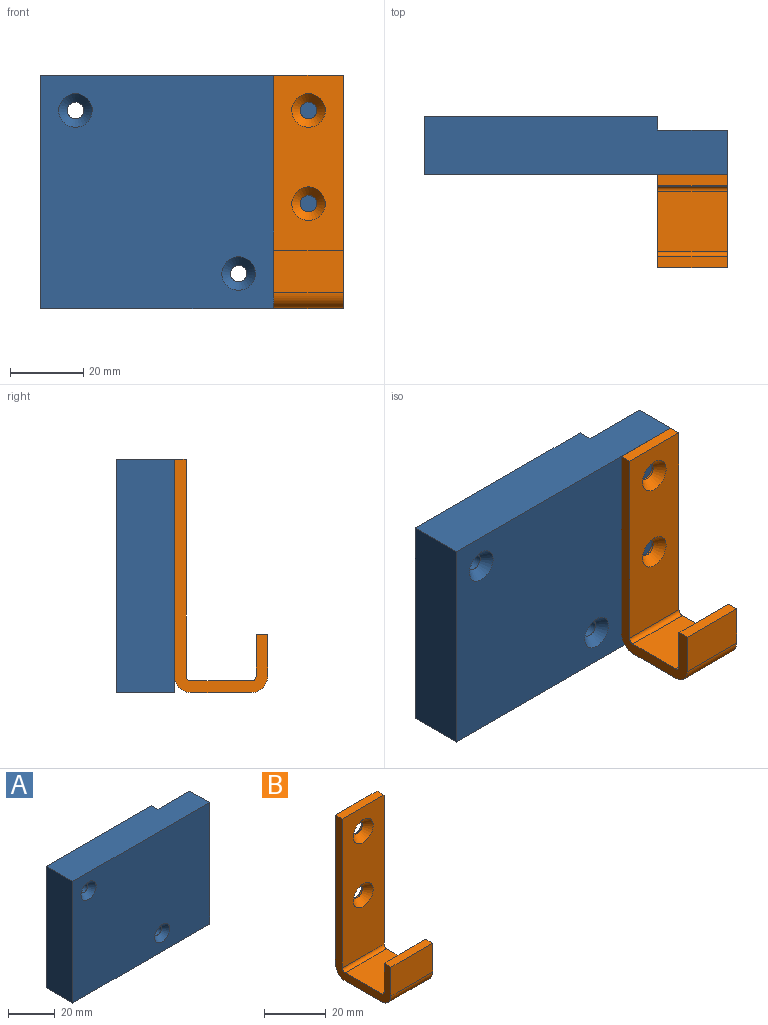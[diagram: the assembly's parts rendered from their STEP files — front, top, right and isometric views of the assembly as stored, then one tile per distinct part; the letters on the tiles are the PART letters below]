
ASSEMBLY  parts=2 mates=1
PART A: 12 faces, bbox 82.6x15.9x63.5 mm
  f0: plane 82.55x15.88mm, normal (0,0,1), area 1237.9mm2, adj f1,f3,f4,f5,f6,f7
  f1: plane 63.5x15.88mm, normal (-1,0,0), area 1008.1mm2, adj f0,f2,f4,f5
  f2: plane 82.55x15.88mm, normal (0,0,-1), area 1237.9mm2, adj f1,f3,f4,f5,f6,f7
  f3: plane 63.5x12.07mm, normal (1,0,0), area 766.1mm2, adj f0,f2,f4,f7
  f4: plane 82.55x63.5mm, normal (0,-1,0), area 5111.3mm2, adj f0,f1,f2,f3,f9,f11
  f5: plane 63.5x63.5mm, normal (0,1,0), area 4000.5mm2, adj f0,f1,f2,f6,f8,f10
  f6: plane 63.5x3.81mm, normal (1,0,0), area 241.9mm2, adj f0,f2,f5,f7
  f7: plane 63.5x19.05mm, normal (0,1,0), area 1209.7mm2, adj f0,f2,f3,f6
  f8: cylinder r=2.25mm len=13.22mm, axis (0,-1,0), area 186.7mm2, adj f5,f9
  f9: cone r=2.25mm half-angle=41deg, axis (0,-1,0), area 75.3mm2, adj f4,f8
  f10: cylinder r=2.25mm len=13.22mm, axis (0,-1,0), area 186.7mm2, adj f5,f11
  f11: cone r=2.25mm half-angle=41deg, axis (0,-1,0), area 75.3mm2, adj f4,f10
PART B: 18 faces, bbox 19.1x25.4x63.5 mm
  f0: cylinder r=1.27mm len=19.05mm, axis (-1,0,0), area 38mm2, adj f1,f11,f12,f13
  f1: plane 19.05x11.43mm, normal (0,1,0), area 217.7mm2, adj f0,f2,f12,f13
  f2: plane 19.05x3.18mm, normal (0,0,1), area 60.5mm2, adj f1,f3,f12,f13
  f3: plane 19.05x11.43mm, normal (0,-1,0), area 217.7mm2, adj f2,f4,f12,f13
  f4: cylinder r=4.45mm len=19.05mm, axis (-1,0,0), area 133mm2, adj f3,f5,f12,f13
  f5: plane 19.05x16.51mm, normal (0,0,-1), area 314.5mm2, adj f4,f6,f12,f13
  f6: cylinder r=4.45mm len=19.05mm, axis (-1,0,0), area 133mm2, adj f5,f7,f12,f13
  f7: plane 59.06x19.05mm, normal (0,1,0), area 1093.2mm2, adj f6,f8,f12,f13,f14,f16
  f8: plane 19.05x3.18mm, normal (0,0,1), area 60.5mm2, adj f7,f9,f12,f13
  f9: plane 59.06x19.05mm, normal (0,-1,0), area 994.4mm2, adj f8,f10,f12,f13,f15,f17
  f10: cylinder r=1.27mm len=19.05mm, axis (-1,0,0), area 38mm2, adj f9,f11,f12,f13
  f11: plane 19.05x16.51mm, normal (0,0,1), area 314.5mm2, adj f0,f10,f12,f13
  f12: plane 63.5x25.4mm, normal (1,0,0), area 304.7mm2, adj f0,f1,f2,f3,f4,f5,f6,f7
  f13: plane 63.5x25.4mm, normal (-1,0,0), area 304.7mm2, adj f0,f1,f2,f3,f4,f5,f6,f7
  f14: cylinder r=2.25mm len=4.5mm, axis (0,-1,0), area 7.3mm2, adj f7,f15
  f15: cone r=2.25mm half-angle=41deg, axis (0,-1,0), area 75.3mm2, adj f9,f14
  f16: cylinder r=2.25mm len=4.5mm, axis (0,-1,0), area 7.3mm2, adj f7,f17
  f17: cone r=2.25mm half-angle=41deg, axis (0,-1,0), area 75.3mm2, adj f9,f16
PLACE A t=(0,-0.69,9.41)mm
PLACE B t=(41.28,-29.26,-19.16)mm
MATE fastened B.f7 <-> A.f4  axis (0,1,0) through (50.8,-16.56,41.16)mm
